# Revit family: GID_R_SP_SW
name_source: partatom
category: Lighting Fixtures
units: mm (PartAtom-declared; Revit-internal decimal feet)

## family parameters
Cut with Voids When Loaded = Yes
Host = Face
Light Source = Yes
Maintain Annotation Orientation = No
Part Type = Normal
Room Calculation Point = No
Round Connector Dimension = Use Diameter
Shared = No

## types (6) — shared parameters
CRI = 70
Color Filter = 16777215
Default Elevation = 6' - 0"
Dimming Lamp Color Temperature Shift = <None>
Input Voltage = 120-347V
Lamp = LED
Load Classification = Lighting
Manufacturer = Above All Lighting
Power Factor = 0.9
Tilt Angle = 90.00°
URL = https://www.abovealllighting.com
Wattage Comments = 2x20W

## per-type parameters (varying)
| type | Beam Angle | Model | Photometric Web File |
| GID-R-20W-3000K-45D-BK | 45.00° | GID-RSP-SW8-45-BK | GID-RSP-SW8-45(2X20W 3000K)_IESNA2002.ies |
| GID-R-20W-4000K-45D-BK | 45.00° | GID-RSP-SW8-45-BK | GID-RSP-SW8-45(2X20W 4000K)_IESNA2002.ies |
| GID-R-20W-5000K-45D-BK | 45.00° | GID-RSP-SW8-45-BK | GID-RSP-SW8-45(2X20W 5000K)_IESNA2002.ies |
| GID-R-20W-5000K-60D-BK | 60.00° | GID-RSP-SW8-60-BK | GID-RSP-SW8-60(2X20W 5000K)_IESNA2002.ies |
| GID-R-20W-4000K-60D-BK | 60.00° | GID-RSP-SW8-60-BK | GID-RSP-SW8-60(2X20W 4000K)_IESNA2002.ies |
| GID-R-20W-3000K-60D-BK | 60.00° | GID-RSP-SW8-60-BK | GID-RSP-SW8-60(2X20W 3000K)_IESNA2002.ies |

## geometry (parser evidence)
native form markers: Sweep x2
no freeform markers — native parametric forms only
